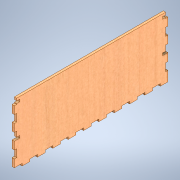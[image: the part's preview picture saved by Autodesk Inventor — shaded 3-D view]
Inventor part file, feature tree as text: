
AUTODESK INVENTOR PART (.ipt)
format: ipt  version: 2021 (Build 250183000, 183)  size: 255,488 bytes
history: native  units: mm
features: extrude x4, sketch x4
ambient origin geometry x8: Origin, YZ Plane, XZ Plane, XY Plane, X Axis, Y Axis, Z Axis, Center Point
bodies: Solid1 (feature_tree)
feature tree (8):
  extrude  "Extrusion1"  Depth=200.0mm
  extrude  "Extrusion2"  Depth=10.0mm
  extrude  "Extrusion3"  Depth=10.0mm
  extrude  "Extrusion4"  Depth=10.0mm
  sketch  "Sketch1"  dims[d0=77.0mm d1=200.0mm]
  sketch  "Sketch2"  dims[d2=3.0mm d3=0.0mm d4=10.0mm]
  sketch  "Sketch3"  dims[d7=100.0mm d9=20.0mm d10=10.0mm d12=10.0mm d14=10.0mm]
  sketch  "Sketch4"  dims[d15=3.0mm d16=10.0mm d17=30.0mm d19=20.0mm d20=10.0mm d22=10.0mm d24=10.0mm d25=10.0mm d26=3.0mm d27=0.0mm d28=10.0mm d29=3.0mm d30=10.0mm d31=20.0mm d32=3.0mm d33=0.0mm d34=4.0mm d35=3.0mm d36=20.0mm d38=190.0mm d39=20.0mm d41=41.0mm d44=0.0mm d45=0.0mm]
